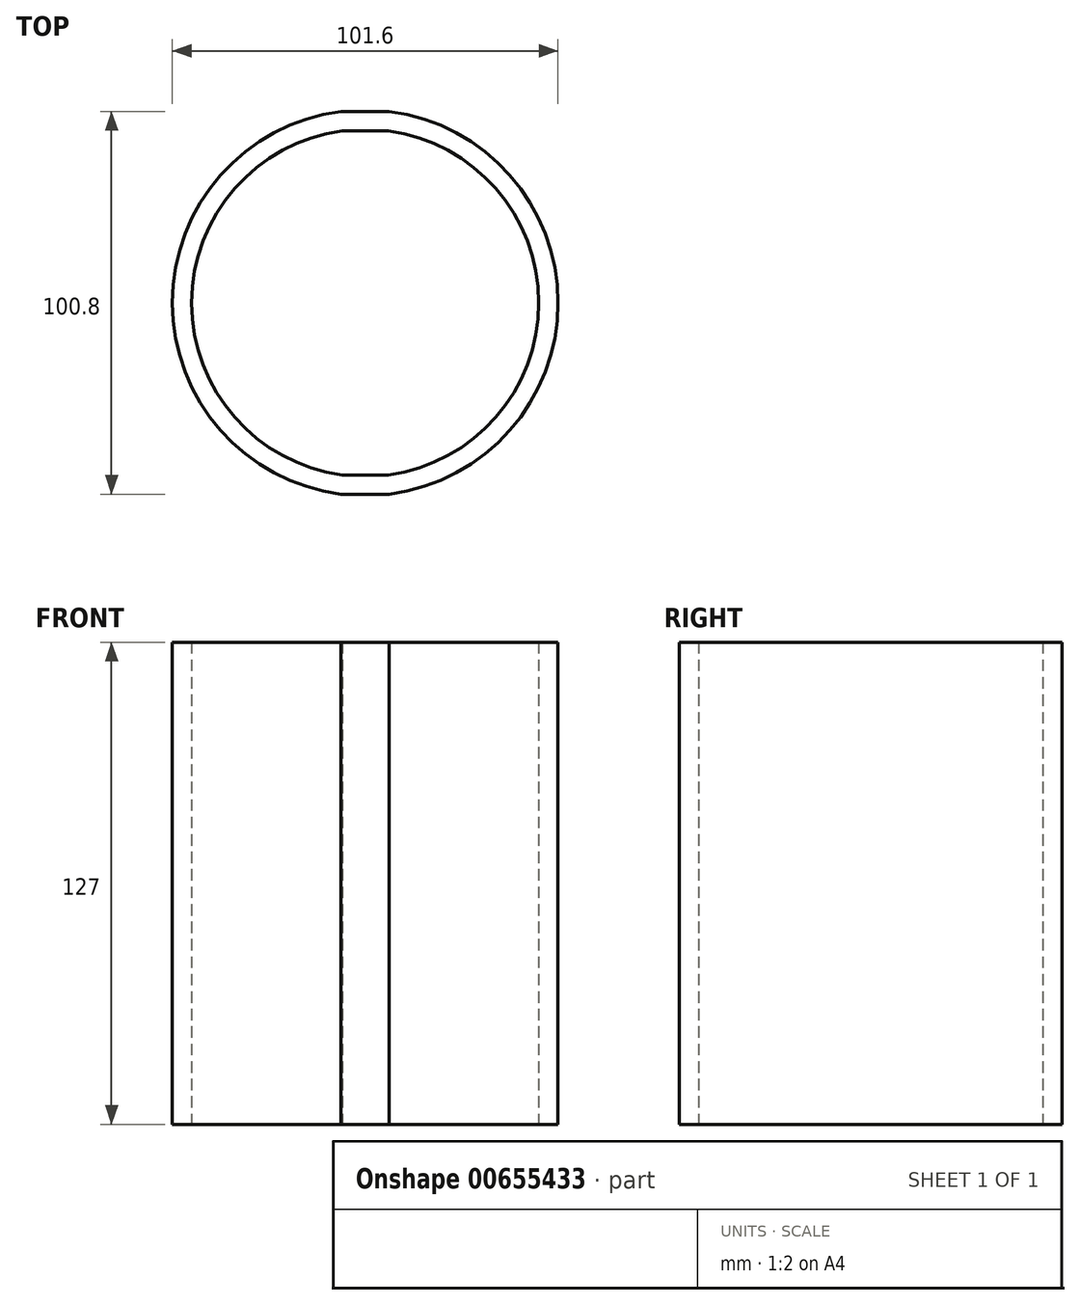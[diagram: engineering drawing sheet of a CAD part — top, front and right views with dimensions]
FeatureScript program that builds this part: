
annotation { "Feature Type Name" : "Feature", "Feature Type Description" : "" }
export const myFeature = defineFeature(function(context is Context, id is Id, definition is map)
    precondition{}
    {
        {
            var Q0;
            Q0=qCreatedBy(makeId("Top.planeOp"),FACE);
            var sketch = newSketch(context, id + "F0", { "sketchPlane" : qUnion([Q0])});
            skArc(sketch, "E0", {"start": v(-6.35, 50.4) * mm, "mid": v(-50.8, 0) * mm, "end": v(-6.35, -50.4) * mm});
            skLineSegment(sketch, "E1", {"start": v(-6.35, -50.4) * mm, "end": v(6.35, -50.4) * mm});
            skLineSegment(sketch, "E2", {"start": v(-6.35, 50.4) * mm, "end": v(6.35, 50.4) * mm});
            skArc(sketch, "E3.trimOffspring", {"start": v(6.35, -50.4) * mm, "mid": v(50.8, 0) * mm, "end": v(6.35, 50.4) * mm});
            skArc(sketch, "E4.0", {"start": v(6.02, -45.32) * mm, "mid": v(45.72, 0) * mm, "end": v(6.02, 45.32) * mm});
            skArc(sketch, "E5.0", {"start": v(-6.02, 45.32) * mm, "mid": v(-45.72, 0) * mm, "end": v(-6.02, -45.32) * mm});
            skLineSegment(sketch, "E6.0", {"start": v(-6.02, 45.32) * mm, "end": v(6.02, 45.32) * mm});
            skLineSegment(sketch, "E7.0", {"start": v(-6.02, -45.32) * mm, "end": v(6.02, -45.32) * mm});
            skSolve(sketch);
        }
        {
            var Q0;
            Q0=makeQuery(id+"F0.imprint","IMPRINT",FACE,{"disambiguationData":[TD([[makeQuery(id+"F0.imprint","IMPRINT",EDGE,{"derivedFrom":sQuery(id+"F0.wireOp",EDGE,"E0")}),1.0]])]});
            extrude(context, id + "F1", {"entities" : qUnion([Q0]), "depth" : 127 * mm, "offsetDistance" : 25.4 * mm});
        }
    });
